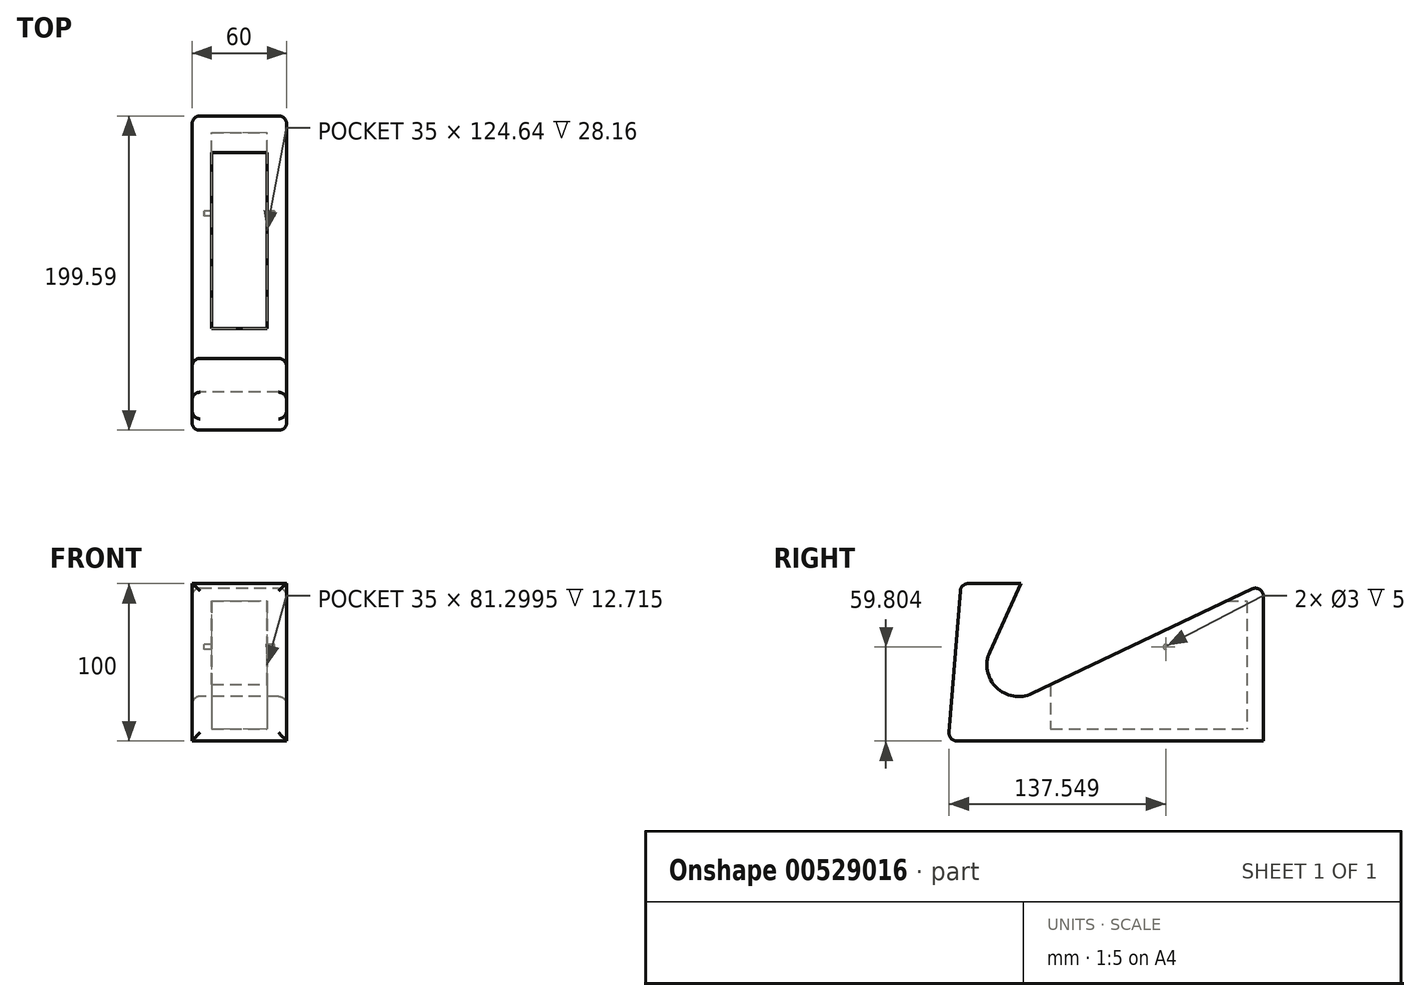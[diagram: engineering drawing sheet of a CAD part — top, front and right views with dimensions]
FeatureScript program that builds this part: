
annotation { "Feature Type Name" : "Feature", "Feature Type Description" : "" }
export const myFeature = defineFeature(function(context is Context, id is Id, definition is map)
    precondition{}
    {
        {
            var Q0;
            Q0=qCreatedBy(makeId("Right.planeOp"),FACE);
            var sketch = newSketch(context, id + "F0", { "sketchPlane" : qUnion([Q0])});
            skLineSegment(sketch, "E0.bottom", {"start": v(100, -47.34) * mm, "end": v(-100, -47.34) * mm});
            skLineSegment(sketch, "E0.top", {"start": v(-53.97, 52.66) * mm, "end": v(-92.15, 52.66) * mm});
            skLineSegment(sketch, "E0.left", {"start": v(100, -47.34) * mm, "end": v(100, 52.66) * mm});
            skPoint(sketch, "E0.middle", {"position": v(0, 2.66) * mm});
            skLineSegment(sketch, "E1", {"start": v(-100, -47.34) * mm, "end": v(-92.15, 52.66) * mm});
            skLineSegment(sketch, "E2", {"start": v(-92.15, 52.66) * mm, "end": v(-53.97, 52.66) * mm});
            skLineSegment(sketch, "E3", {"start": v(-53.97, 52.66) * mm, "end": v(-73.73, 9.24) * mm});
            skLineSegment(sketch, "E4", {"start": v(-46.95, -17.11) * mm, "end": v(100, 52.66) * mm});
            skPoint(sketch, "E0.right.end.orphan", {"position": v(-100, 52.66) * mm});
            skPoint(sketch, "E5.visualSharp", {"position": v(-96.41, -40.6) * mm});
            skArc(sketch, "E5.filletArc", {"start": v(-73.73, 9.24) * mm, "mid": v(-69.56, -13.3) * mm, "end": v(-46.95, -17.11) * mm});
            skSolve(sketch);
        }
        {
            var Q0;
            Q0 = qSketchRegion(id + "F0", true);
            extrude(context, id + "F1", {"entities" : qUnion([Q0]), "endBound" : BoundingType.SYMMETRIC, "depth" : 60 * mm, "offsetDistance" : 25 * mm});
        }
        {
            var Q0;
            Q0=makeQuery(id+"F1.opExtrude","SWEPT_EDGE",EDGE,{"disambiguationData":[OSD([sQuery(id+"F0.wireOp",EDGE,"E1"),sQuery(id+"F0.wireOp",EDGE,"E2")])]});
            var Q1;
            Q1=makeQuery(id+"F1.opExtrude","SWEPT_EDGE",EDGE,{"disambiguationData":[OSD([sQuery(id+"F0.wireOp",EDGE,"E0.left"),sQuery(id+"F0.wireOp",EDGE,"E4")])]});
            var Q2;
            Q2=makeQuery(id+"F1.opExtrude","CAP_EDGE",EDGE,{"disambiguationData":[OSD([sQuery(id+"F0.wireOp",EDGE,"E4")])],"isStart":false});
            var Q3;
            Q3=makeQuery(id+"F1.opExtrude","CAP_EDGE",EDGE,{"disambiguationData":[OSD([sQuery(id+"F0.wireOp",EDGE,"E4")])],"isStart":true});
            var Q4;
            Q4=makeQuery(id+"F1.opExtrude","CAP_EDGE",EDGE,{"disambiguationData":[OSD([sQuery(id+"F0.wireOp",EDGE,"E0.left")])],"isStart":false});
            var Q5;
            Q5=makeQuery(id+"F1.opExtrude","CAP_EDGE",EDGE,{"disambiguationData":[OSD([sQuery(id+"F0.wireOp",EDGE,"E0.left")])],"isStart":true});
            var Q6;
            Q6=makeQuery(id+"F1.opExtrude","CAP_EDGE",EDGE,{"disambiguationData":[OSD([sQuery(id+"F0.wireOp",EDGE,"E1")])],"isStart":false});
            var Q7;
            Q7=makeQuery(id+"F1.opExtrude","CAP_EDGE",EDGE,{"disambiguationData":[OSD([sQuery(id+"F0.wireOp",EDGE,"E1")])],"isStart":true});
            fillet(context, id + "F2", {"entities" : qUnion([Q0, Q1, Q2, Q3, Q4, Q5, Q6, Q7]), "radius" : 5 * mm, "tangentPropagation" : true, "allowEdgeOverflow" : false});
        }
        {
            var Q0;
            Q0=qCreatedBy(makeId("Right.planeOp"),FACE);
            var sketch = newSketch(context, id + "F3", { "sketchPlane" : qUnion([Q0])});
            skLineSegment(sketch, "E6.bottom", {"start": v(-35.13, 41.64) * mm, "end": v(89.51, 41.64) * mm});
            skLineSegment(sketch, "E6.top", {"start": v(-35.13, -39.66) * mm, "end": v(89.51, -39.66) * mm});
            skLineSegment(sketch, "E6.left", {"start": v(-35.13, 41.64) * mm, "end": v(-35.13, -39.66) * mm});
            skLineSegment(sketch, "E6.right", {"start": v(89.51, 41.64) * mm, "end": v(89.51, -39.66) * mm});
            skSolve(sketch);
        }
        {
            var Q0;
            Q0 = qSketchRegion(id + "F3", true);
            extrude(context, id + "F4", {"entities" : qUnion([Q0]), "operationType" : NewBodyOperationType.REMOVE, "endBound" : BoundingType.SYMMETRIC, "oppositeDirection" : true, "depth" : 35 * mm, "offsetDistance" : 25 * mm});
        }
        {
            var Q0;
            Q0=qCreatedBy(makeId("Right.planeOp"),FACE);
            var sketch = newSketch(context, id + "F5", { "sketchPlane" : qUnion([Q0])});
            skCircle(sketch, "E7", {"center": v(37.96, 12.46) * mm, "radius": 1.5 * mm});
            skSolve(sketch);
        }
        {
            var Q0;
            Q0 = qSketchRegion(id + "F5", true);
            extrude(context, id + "F6", {"entities" : qUnion([Q0]), "operationType" : NewBodyOperationType.REMOVE, "endBound" : BoundingType.SYMMETRIC, "depth" : 45 * mm, "offsetDistance" : 25 * mm});
        }
    });
